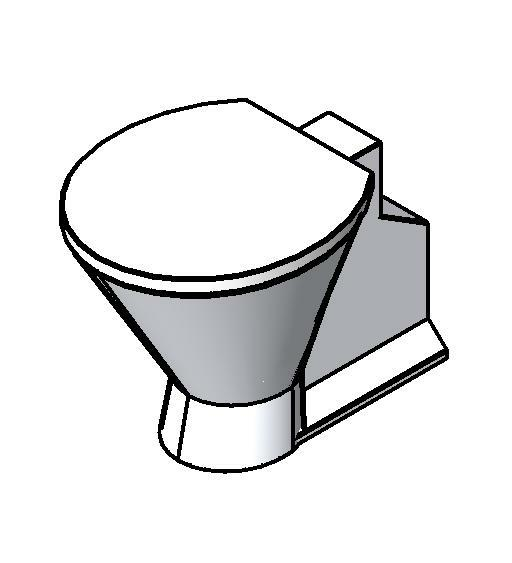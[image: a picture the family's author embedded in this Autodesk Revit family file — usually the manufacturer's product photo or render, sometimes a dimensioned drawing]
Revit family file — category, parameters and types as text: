
# Revit family: Deca_Acionamento monocomando mesa redonda_Deca You_4990.104
name_source: partatom
category: Plumbing Fixtures
units: mm (PartAtom-declared; Revit-internal decimal feet)

## family parameters
Cut with Voids When Loaded = No
Host = Face
Part Type = Normal
Room Calculation Point = No
Round Connector Dimension = Use Radius
Shared = No

## types (11) — shared parameters
Acompanha o Produto = Flexiveis e Adaptadores de Rosca
Aprovado por = quattroD
Atendimento ao Cliente = 0800-0117073
Categoria = Acionamento  Monoc Lavatório / Banheiro
Composição Básica = Liga de Cobre (Latão),Plásticos de Engenharia, Aço Inoxidavel e Elastômeros
Consumo = -
Cor Secundária = -
Criado por = quattroD
Itens de Instalação = Mangueira Flexivel
Linha = Deca You
Manufacturer = DECA
Norma = Não possui
Pressão mín. Aquec. Acúmulo = -
Pressão mín. Aquec. Passagem = -
Saída de Esgoto = -
Segmento = Luxo
Tipo de dispositivo economizador = -
Tipo de mecanismo utilizado = Cartucho moncomando Rotativo
Tipo de rosca de entrada = BSP
Tipo de rosca de saída = BSP
URL = www.deca.com.br
zero-valued in all types: CWFU, Default Elevation, Diâmetro Ponto de Esgoto, Diâmetro Água Fria, Peso Líquido (Kg), Raio Ponto de Esgoto, Raio Água Fria, WFU

## per-type parameters (varying)
| type | Cor Principal | Código Pai | Material | Model |
| 4990.C104_Cromado | Cromado | 4990.C104 | Deca_Cromado | 4990.C104 |
| 4990.BL104.MT_Black Matte | Black Matte | 4990.BL104.MT | Deca_Black Matte | 4990.BL104.MT |
| 4990.GF104.MT_Grafite | Antracite Dark | 4990.GF104.MT | Deca_Grafite | 4990.GF104.MT |
| 4990.INX104_Inox | Inox | 4990.INX104 | Deca_Inox | 4990.INX104 |
| 4990.MR104.MT_Brown Matte | BROWN MATTE | 4990.MR104.MT | Deca_Brown Matte | 4990.MR104.MT |
| 4990.SM104.MT_Summer Gold | SUMMER GOLD | 4990.SM104.MT | Deca_Summer Gold | 4990.SM104.MT |
| 4990.BR104.MT_Dynamic White | Dynamic White | 4990.BR104.MT | Deca_Dynamic White | 4990.BR104.MT |
| 4990.LS104.MT_Dynamic Gold | Dynamic Gold | 4990.LS104.MT | Deca_Dynamic Gold | 4990.LS104.MT |
| 4990.CL104.MT_Dynamic Peach | Dynamic Peach | 4990.CL104.MT | Deca_Dynamic Peach | 4990.CL104.MT |
| 4990.LV104.MT_Dynamic Lilac | Dynamic Lilac | 4990.LV104.MT | Deca_Dynamic Lilac | 4990.LV104.MT |
| 4990.AZ104.MT_Dynamic Blue | Dynamic Blue | 4990.AZ104.MT | Deca_Dynamic Blue | 4990.AZ104.MT |

## geometry (parser evidence)
native form markers: Sweep x2
no freeform markers — native parametric forms only
